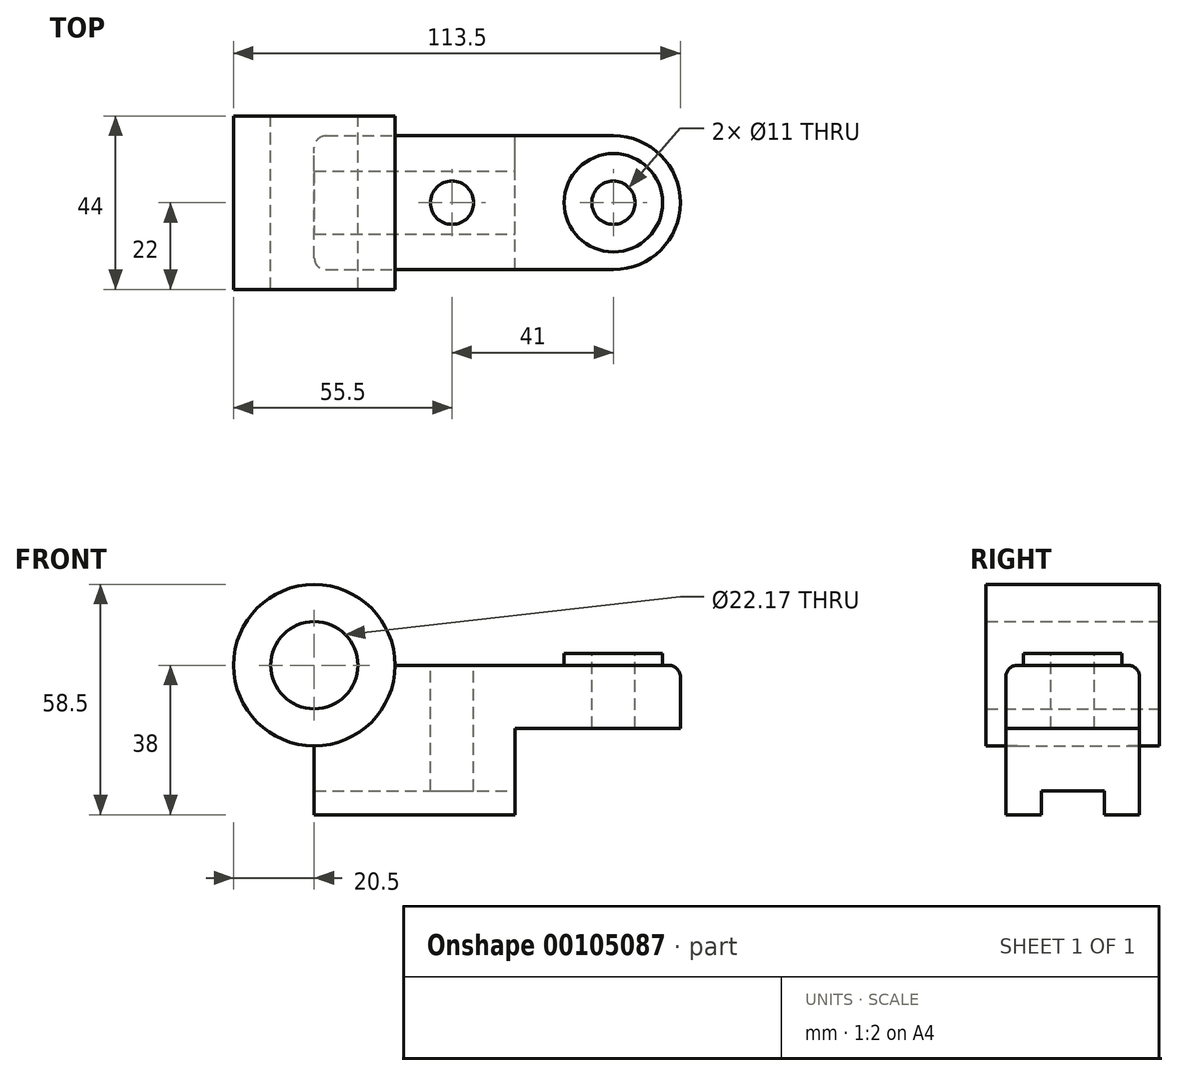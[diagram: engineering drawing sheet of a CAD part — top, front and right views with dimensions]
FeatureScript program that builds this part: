
annotation { "Feature Type Name" : "Feature", "Feature Type Description" : "" }
export const myFeature = defineFeature(function(context is Context, id is Id, definition is map)
    precondition{}
    {
        {
            var Q0;
            Q0=qCreatedBy(makeId("Front.planeOp"),FACE);
            var sketch = newSketch(context, id + "F0", { "sketchPlane" : qUnion([Q0])});
            skLineSegment(sketch, "E0.bottom", {"start": v(0, 0) * mm, "end": v(51, 0) * mm});
            skLineSegment(sketch, "E0.top", {"start": v(0, 38) * mm, "end": v(76, 38) * mm});
            skLineSegment(sketch, "E0.left", {"start": v(0, 0) * mm, "end": v(0, 38) * mm});
            skLineSegment(sketch, "E0.right", {"start": v(76, 22) * mm, "end": v(76, 38) * mm});
            skLineSegment(sketch, "E1.top", {"start": v(51, 22) * mm, "end": v(76, 22) * mm});
            skLineSegment(sketch, "E1.left", {"start": v(51, 0) * mm, "end": v(51, 22) * mm});
            skCircle(sketch, "E2", {"center": v(0, 38) * mm, "radius": 11.09 * mm});
            skCircle(sketch, "E3", {"center": v(0, 38) * mm, "radius": 20.5 * mm});
            skSolve(sketch);
        }
        {
            var Q0;
            {var subQ2=sQuery(id+"F0.wireOp",EDGE,"E0.bottom");Q0=makeQuery(id+"F0.imprint","IMPRINT",FACE,{"disambiguationData":[TD([[makeQuery(id+"F0.imprint","IMPRINT",EDGE,{"derivedFrom":subQ2}),1.0]])]});}
            extrude(context, id + "F1", {"entities" : qUnion([Q0]), "endBound" : BoundingType.SYMMETRIC, "depth" : (17 * 2) * mm});
        }
        {
            var Q0;
            {var subQ0=sQuery(id+"F0.wireOp",EDGE,"E3");var subQ1=sQuery(id+"F0.wireOp",EDGE,"E0.top");var subQ2=makeQuery(id+"F0.imprint","INTERSECT",VERTEX,{"derivedFrom":[subQ1,subQ0]});Q0=makeQuery(id+"F0.imprint","IMPRINT",FACE,{"disambiguationData":[TD([[makeQuery(id+"F0.imprint","IMPRINT",EDGE,{"disambiguationData":[TD([[subQ2,1.0]])],"derivedFrom":subQ1}),1.0]])]});}
            var Q1;
            {var subQ0=sQuery(id+"F0.wireOp",EDGE,"E3");var subQ1=sQuery(id+"F0.wireOp",EDGE,"E0.top");var subQ2=makeQuery(id+"F0.imprint","INTERSECT",VERTEX,{"derivedFrom":[subQ1,subQ0]});Q1=makeQuery(id+"F0.imprint","IMPRINT",FACE,{"disambiguationData":[TD([[makeQuery(id+"F0.imprint","IMPRINT",EDGE,{"disambiguationData":[TD([[subQ2,1.0]])],"derivedFrom":subQ1}),-1.0]])]});}
            extrude(context, id + "F2", {"entities" : qUnion([Q0, Q1]), "operationType" : NewBodyOperationType.ADD, "endBound" : BoundingType.SYMMETRIC, "depth" : 44 * mm});
        }
        {
            var Q0;
            Q0=makeQuery(id+"F1.opExtrude","SWEPT_FACE",FACE,{"disambiguationData":[OSD([sQuery(id+"F0.wireOp",EDGE,"E0.top")])]});
            var sketch = newSketch(context, id + "F3", { "sketchPlane" : qUnion([Q0])});
            skArc(sketch, "E4", {"start": v(76, -17) * mm, "mid": v(93, 0) * mm, "end": v(76, 17) * mm});
            skSolve(sketch);
        }
        {
            var Q0;
            Q0=makeQuery(id+"F3.imprint","IMPRINT",FACE,{"disambiguationData":[TD([[makeQuery(id+"F3.imprint","IMPRINT",EDGE,{"derivedFrom":sQuery(id+"F3.wireOp",EDGE,"E4")}),1.0]])]});
            var Q1;
            Q1=makeQuery(id+"F1.opExtrude","SWEPT_FACE",FACE,{"disambiguationData":[OSD([sQuery(id+"F0.wireOp",EDGE,"E1.top")])]});
            extrude(context, id + "F4", {"entities" : qUnion([Q0]), "operationType" : NewBodyOperationType.ADD, "endBound" : BoundingType.UP_TO_SURFACE, "oppositeDirection" : true, "endBoundEntityFace" : qUnion([Q1]), "depth" : 25 * mm});
        }
        {
            var Q0;
            {var subQ0=sQuery(id+"F0.wireOp",EDGE,"E0.top");Q0=makeQuery(id+"F4.boolean.opBoolean","MERGE",FACE,{"derivedFrom":[makeQuery(id+"F1.opExtrude","SWEPT_FACE",FACE,{"disambiguationData":[OSD([subQ0])]}),makeQuery(id+"F4.opExtrude","CAP_FACE",FACE,{"disambiguationData":[OSD([subQ0,sQuery(id+"F0.wireOp",EDGE,"E0.right"),sQuery(id+"F3.wireOp",EDGE,"E4")])],"isStart":true})]});}
            var sketch = newSketch(context, id + "F5", { "sketchPlane" : qUnion([Q0])});
            skCircle(sketch, "E5", {"center": v(76, 0) * mm, "radius": 12.5 * mm});
            skSolve(sketch);
        }
        {
            var Q0;
            Q0=makeQuery(id+"F5.imprint","IMPRINT",FACE,{"disambiguationData":[TD([[makeQuery(id+"F5.imprint","IMPRINT",EDGE,{"derivedFrom":sQuery(id+"F5.wireOp",EDGE,"E5")}),1.0]])]});
            extrude(context, id + "F6", {"entities" : qUnion([Q0]), "operationType" : NewBodyOperationType.ADD, "depth" : 3 * mm});
        }
        {
            var Q0;
            Q0=makeQuery(id+"F6.opExtrude","CAP_FACE",FACE,{"disambiguationData":[OSD([sQuery(id+"F5.wireOp",EDGE,"E5")])],"isStart":false});
            var sketch = newSketch(context, id + "F7", { "sketchPlane" : qUnion([Q0])});
            skCircle(sketch, "E6", {"center": v(76, 0) * mm, "radius": 5.5 * mm});
            skCircle(sketch, "E7", {"center": v(35, 0) * mm, "radius": 5.5 * mm});
            skSolve(sketch);
        }
        {
            var Q0;
            Q0 = qSketchRegion(id + "F7", true);
            extrude(context, id + "F8", {"entities" : qUnion([Q0]), "operationType" : NewBodyOperationType.REMOVE, "endBound" : BoundingType.THROUGH_ALL, "oppositeDirection" : true, "depth" : 25 * mm});
        }
        {
            var Q0;
            Q0=makeQuery(id+"F1.opExtrude","SWEPT_FACE",FACE,{"disambiguationData":[OSD([sQuery(id+"F0.wireOp",EDGE,"E1.left")])]});
            var sketch = newSketch(context, id + "F9", { "sketchPlane" : qUnion([Q0])});
            skLineSegment(sketch, "E8.bottom", {"start": v(-8, 0) * mm, "end": v(8, 0) * mm});
            skLineSegment(sketch, "E8.top", {"start": v(-8, 6) * mm, "end": v(8, 6) * mm});
            skLineSegment(sketch, "E8.left", {"start": v(-8, 0) * mm, "end": v(-8, 6) * mm});
            skLineSegment(sketch, "E8.right", {"start": v(8, 0) * mm, "end": v(8, 6) * mm});
            skSolve(sketch);
        }
        {
            var Q0;
            Q0 = qSketchRegion(id + "F9", true);
            extrude(context, id + "F10", {"entities" : qUnion([Q0]), "operationType" : NewBodyOperationType.REMOVE, "endBound" : BoundingType.THROUGH_ALL, "oppositeDirection" : true, "depth" : 25 * mm});
        }
        {
            var Q0;
            Q0=makeQuery(id+"F6.opExtrude","CAP_EDGE",EDGE,{"disambiguationData":[OSD([sQuery(id+"F5.wireOp",EDGE,"E5")])],"isStart":true});
            var Q1;
            Q1=makeQuery(id+"F1.opExtrude","CAP_EDGE",EDGE,{"disambiguationData":[OSD([sQuery(id+"F0.wireOp",EDGE,"E3")])],"isStart":false});
            var Q2;
            Q2=makeQuery(id+"F1.opExtrude","CAP_EDGE",EDGE,{"disambiguationData":[OSD([sQuery(id+"F0.wireOp",EDGE,"E3")])],"isStart":true});
            var Q3;
            Q3=makeQuery(id+"F1.opExtrude","SWEPT_EDGE",EDGE,{"disambiguationData":[OSD([sQuery(id+"F0.wireOp",EDGE,"E0.left"),sQuery(id+"F0.wireOp",EDGE,"E3")])]});
            var Q4;
            Q4=makeQuery(id+"F1.opExtrude","SWEPT_EDGE",EDGE,{"disambiguationData":[OSD([sQuery(id+"F0.wireOp",EDGE,"E0.top"),sQuery(id+"F0.wireOp",EDGE,"E3")])]});
            var Q5;
            Q5=makeQuery(id+"F1.opExtrude","CAP_EDGE",EDGE,{"disambiguationData":[OSD([sQuery(id+"F0.wireOp",EDGE,"E0.left")])],"isStart":false});
            var Q6;
            Q6=makeQuery(id+"F1.opExtrude","CAP_EDGE",EDGE,{"disambiguationData":[OSD([sQuery(id+"F0.wireOp",EDGE,"E0.left")])],"isStart":true});
            fillet(context, id + "F11", {"entities" : qUnion([Q0, Q1, Q2, Q3, Q4, Q5, Q6]), "radius" : 3 * mm, "tangentPropagation" : true, "allowEdgeOverflow" : false});
        }
        {
            var Q0;
            Q0=makeQuery(id+"F1.opExtrude","CAP_EDGE",EDGE,{"disambiguationData":[OSD([sQuery(id+"F0.wireOp",EDGE,"E0.top")])],"isStart":false});
            fillet(context, id + "F12", {"entities" : qUnion([Q0]), "radius" : 3 * mm, "tangentPropagation" : true, "allowEdgeOverflow" : false});
        }
    });
